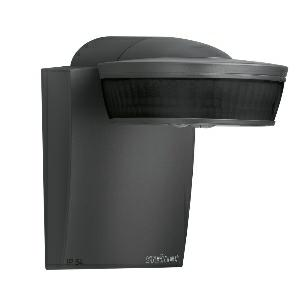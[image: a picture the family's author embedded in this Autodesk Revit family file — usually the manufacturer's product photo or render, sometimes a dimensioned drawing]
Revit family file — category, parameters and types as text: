
# Revit family: sensiq_056636
name_source: partatom
category: Elektroinstallationen
revit_build: Autodesk Revit 2016 (Build: 20190508_0715(x64)
units: mm (PartAtom-declared; Revit-internal decimal feet)

## family parameters
Basisbauteil = Fläche
Beim Laden mit Abzugskörper schneiden = Nein
Bemaßung runder Anschluss = Durchmesser verwenden
Beschriftungsausrichtung beibehalten = Nein
Gemeinsam genutzt = Nein
Raumberechnungspunkt = Nein
Teiletyp = Normal

## types (1)
- sensIQ
    Apparent Load = 0 VA
    Beschreibung = Type: Motion detectors; Type of accessory: Corner adapter; Dimensions (L x W x H): 172 x 113 x 144 mm; Mains power supply: 230 V / 50 – 60 Hz; Sensor Technology: passive infrared; Application, place: Indoors, Outdoors; Application, room: multi-storey / underground car park, outdoors, warehouse, front door, all round the building, courtyard & driveway, Indoors; Installation site: wall, ceiling, corner; Installation: Surface wiring; Switching zones: 1360 switching zones; Electronic scalability: No; Mechanical scalability: Yes; Mounting height: 2,00 – 5,00 m; Optimum mounting height: 2 m; Detection angle: 300 °; Angle of aperture: 90 °; Sneak-by guard: Yes; Capability of masking out individual segments: Yes; Reach, detail: Reach adjustable from 2 - 20 m in 3 directions (100° in each); Reach, radial: r = 4 m (42 m²); Reach, tangential: r = 20 m (1047 m²); Twilight setting TEACH: Yes; Twilight setting: 2 – 2000 lx; Time setting: 5 sec – 15 min; Constant-lighting control: No; Basic light level function: No; Functions: Normal / test mode, Manual ON / ON-OFF; Settings via: Remote control, Potentiometers, Smart Remote; With remote control: Yes; Interconnection: Yes; IP-rating: IP54; Material: Plastic; Ambient temperature: -20 – 50 °C; Colour: Anthracite; IDs, certificates: VDE; Manufacturer's Warranty: 5 years; Version: Anthracite; PU1, EAN: 4007841056636
    Height = 144 mm
    Hersteller = Steinel
    Length = 172 mm
    Maximum range = 22.149 m
    ModVariant = Nein
    Modell = 056636
    Mounting Type = Surface mounted
    Number of Poles = 1
    OnlyDefault = Ja
    Power Factor = 1
    Product Name = sensIQ
    Product group = Sensor-switched indoor light
    ProductGroupID = 30
    Protection Class = Protection class
    Protection Degree = IP 54
    RlxData = <blob elided: 187409 chars, md5=db86e4a0>
    Sensor characteristics = Semi circular 145°-300°
    Sensor type = Passive (infrared)
    SensorDataFile = <blob elided: 9086 chars, md5=cfd8d4b9>
    Type of entry = Motion
    Typenbild = produkt1_056636.jpg
    Typenkommentare = Product without accessories
    URL = http://relux.com
    VarID = ---
    Voltage = 0 V
    Vorgabe-Ansicht = 1800 mm
    Weight = 0.00 kg
    Width = 113 mm

## geometry (parser evidence)
native form markers: Blend x4, Sweep x19
no freeform markers — native parametric forms only
